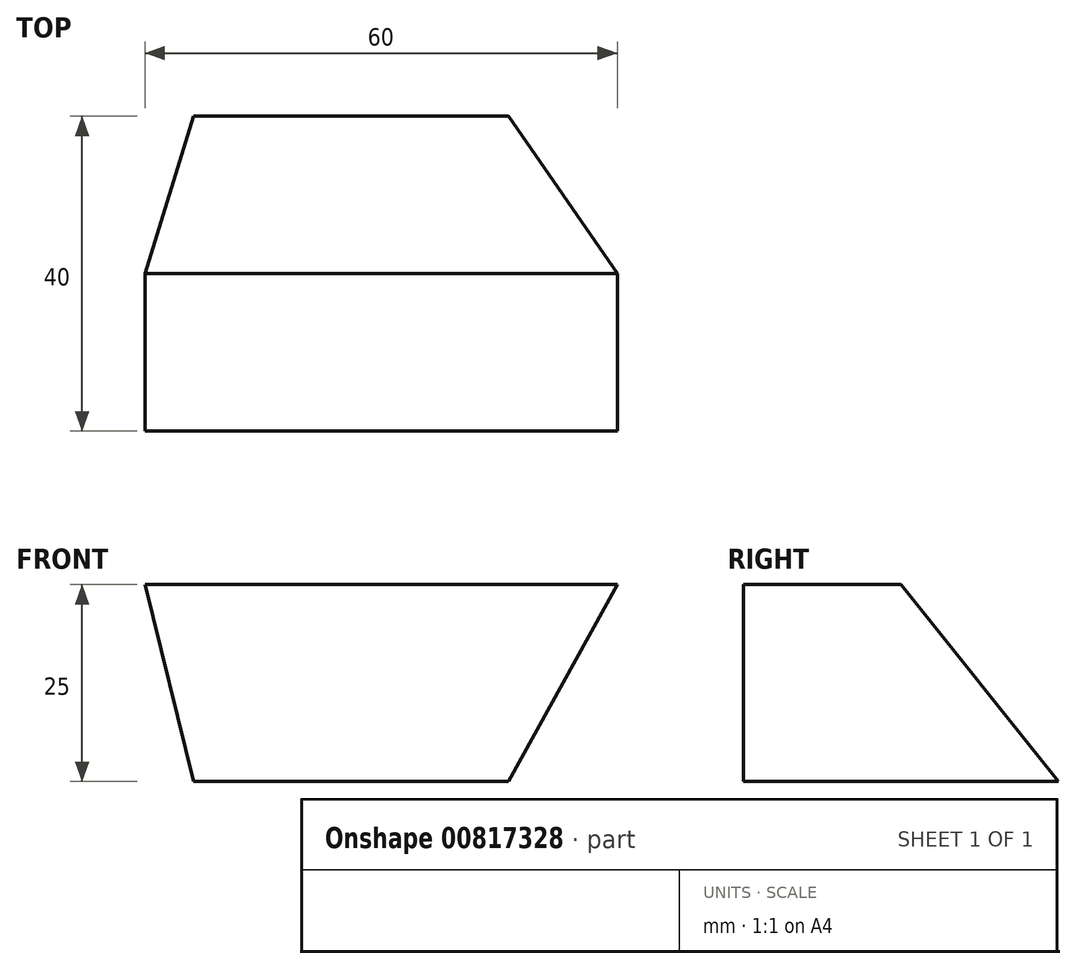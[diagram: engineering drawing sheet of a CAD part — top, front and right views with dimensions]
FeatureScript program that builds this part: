
annotation { "Feature Type Name" : "Feature", "Feature Type Description" : "" }
export const myFeature = defineFeature(function(context is Context, id is Id, definition is map)
    precondition{}
    {
        {
            var Q0;
            Q0=qCreatedBy(makeId("Top.planeOp"),FACE);
            var sketch = newSketch(context, id + "F0", { "sketchPlane" : qUnion([Q0])});
            skLineSegment(sketch, "E0.bottom", {"start": v(0, 40) * mm, "end": v(-40, 40) * mm});
            skLineSegment(sketch, "E0.top", {"start": v(0, 0) * mm, "end": v(-40, 0) * mm});
            skLineSegment(sketch, "E0.left", {"start": v(0, 40) * mm, "end": v(0, 0) * mm});
            skLineSegment(sketch, "E0.right", {"start": v(-40, 40) * mm, "end": v(-40, 0) * mm});
            skSolve(sketch);
        }
        {
            var Q0;
            Q0=qCreatedBy(makeId("Top.planeOp"),FACE);
            cPlane(context, id + "F1", {"entities" : qUnion([Q0]), "cplaneType" : CPlaneType.OFFSET, "offset" : 25 * mm, "width" : 150 * mm, "height" : 150 * mm});
        }
        {
            var Q0;
            Q0=qCreatedBy(id+"F1.planeOp",FACE);
            var sketch = newSketch(context, id + "F2", { "sketchPlane" : qUnion([Q0])});
            skLineSegment(sketch, "E1.bottom", {"start": v(-46.17, 0) * mm, "end": v(13.83, 0) * mm});
            skLineSegment(sketch, "E1.top", {"start": v(-46.17, 20) * mm, "end": v(13.83, 20) * mm});
            skLineSegment(sketch, "E1.left", {"start": v(-46.17, 0) * mm, "end": v(-46.17, 20) * mm});
            skLineSegment(sketch, "E1.right", {"start": v(13.83, 0) * mm, "end": v(13.83, 20) * mm});
            skSolve(sketch);
        }
        {
            var Q0;
            Q0=makeQuery(id+"F0.imprint","IMPRINT",FACE,{"disambiguationData":[TD([[makeQuery(id+"F0.imprint","IMPRINT",EDGE,{"derivedFrom":sQuery(id+"F0.wireOp",EDGE,"E0.bottom")}),1.0]])]});
            var Q1;
            Q1=makeQuery(id+"F2.imprint","IMPRINT",FACE,{"disambiguationData":[TD([[makeQuery(id+"F2.imprint","IMPRINT",EDGE,{"derivedFrom":sQuery(id+"F2.wireOp",EDGE,"E1.bottom")}),1.0]])]});
            loft(context, id + "F3", {"sheetProfilesArray" : [{ "sheetProfileEntities" : qUnion([Q0]) }, { "sheetProfileEntities" : qUnion([Q1]) }]});
        }
    });
